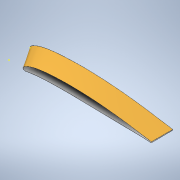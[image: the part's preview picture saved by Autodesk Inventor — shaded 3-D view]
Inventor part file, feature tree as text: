
AUTODESK INVENTOR PART (.ipt)
format: ipt  version: 2022 (Build 260153000, 153)  size: 573,952 bytes
history: native  units: mm
features: sketch x9, plane x1, loft x1
ambient origin geometry x8: Origin, YZ Plane, XZ Plane, XY Plane, X Axis, Y Axis, Z Axis, Center Point
bodies: Body1 (feature_tree)
feature tree (11):
  sketch  "Sketch3"  dims[d29=150.0mm d35=2.0mm]
  sketch  "Sketch4"  dims[d36=90.0deg]
  sketch  "Sketch5"  dims[d37=2.0mm]
  sketch  "Sketch6"  dims[d38=90.0deg]
  plane  "Work Plane2"
  sketch  "Sketch9"  dims[d43=2.0mm]
  sketch  "Sketch10"  dims[d44=2.0mm]
  sketch  "Sketch16"  dims[d51=2.0mm]
  sketch  "Sketch17"  dims[d52=2.0mm]
  sketch  "Sketch18"  dims[d56=2.0mm d57=2.0mm d65=2.0mm d66=2.0mm d69=2.0mm d70=2.0mm d76=2.0mm d77=0.0mm d150=1.8mm d151=1.8mm d156=1.8mm d157=1.8mm d167=1.8mm d168=90.0deg d169=1.8mm d170=90.0deg d175=1.8mm d176=1.8mm d187=1.8mm d188=1.8mm d193=1.8mm d194=90.0deg d195=1.8mm d196=90.0deg d205=1.000001mm d206=0.99998mm d207=0.0mm d208=90.0deg d209=0.0mm d210=90.0deg d6=0.5mm d7=0.872665mm d8=0.5mm d9=0.872665mm]
  loft  "Loft2"
